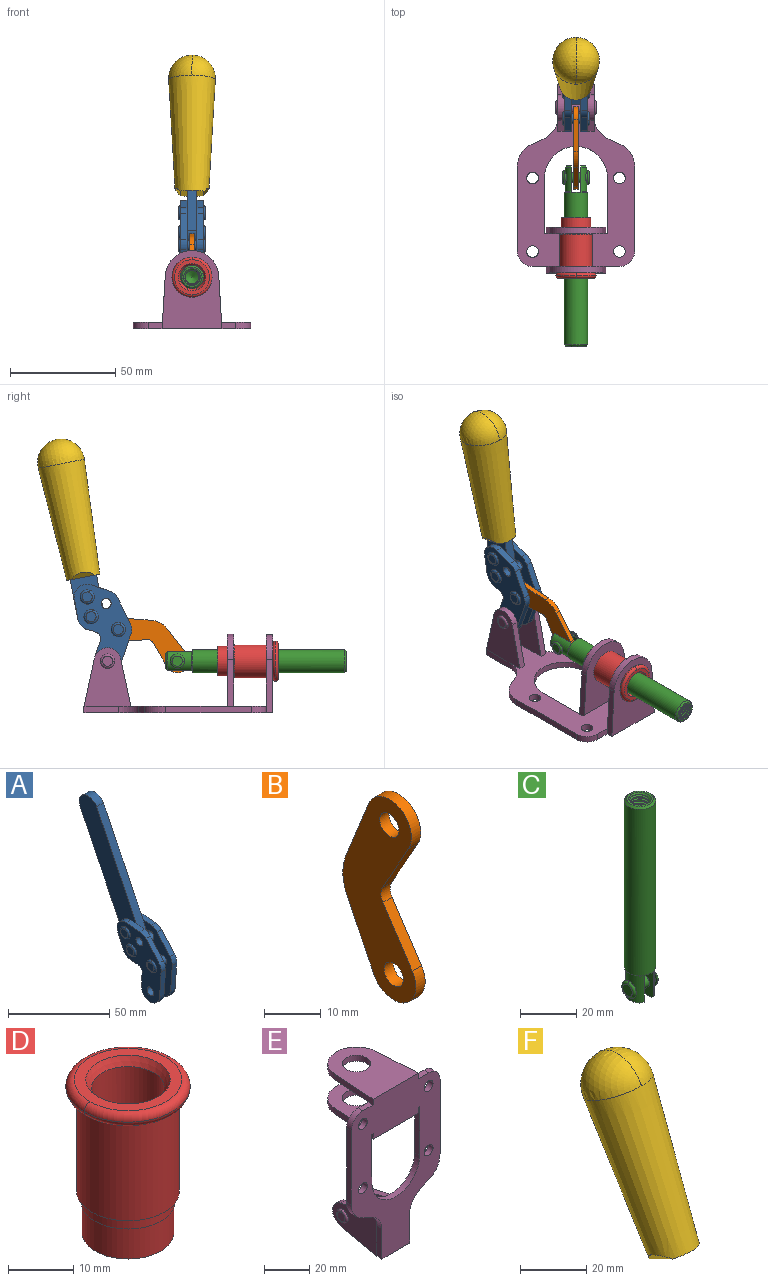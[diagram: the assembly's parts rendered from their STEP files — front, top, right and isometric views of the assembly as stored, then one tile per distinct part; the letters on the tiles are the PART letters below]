
ASSEMBLY  parts=6 mates=6
PART A: 59 faces, bbox 12.9x60.2x99.6 mm
  f0: torus R=2.39mm, axis (-1,0,0), area 14.9mm2, adj f20,f43,f51
  f1: torus R=2.39mm, axis (-1,0,0), area 14.9mm2, adj f19,f42,f51
  f2: torus R=2.39mm, axis (-1,0,0), area 14.9mm2, adj f18,f35,f51
  f3: torus R=2.39mm, axis (-1,0,0), area 14.9mm2, adj f14,f17,f23
  f4: torus R=2.39mm, axis (-1,0,0), area 14.9mm2, adj f13,f16,f23
  f5: torus R=2.39mm, axis (-1,0,0), area 14.9mm2, adj f12,f15,f23
  f6: cylinder r=2.39mm len=4.78mm, axis (1,0,0), area 46.5mm2, adj f48,f50,f51
  f7: cylinder r=2.39mm len=4.78mm, axis (1,0,0), area 46.5mm2, adj f50,f51
  f8: cylinder r=6.35mm len=12.68mm, axis (1,0,0), area 61.8mm2, adj f38,f39,f50,f51
  f9: cylinder r=2.39mm len=4.78mm, axis (-1,0,0), area 70.5mm2, adj f46,f50
  f10: cylinder r=2.39mm len=4.78mm, axis (-1,0,0), area 46.5mm2, adj f23,f45,f46
  f11: cylinder r=2.39mm len=4.78mm, axis (-1,0,0), area 46.5mm2, adj f23,f46
  f12: plane 4.78x4.78mm, normal (1,0,0), area 17.9mm2, adj f5,f15
  f13: plane 4.78x4.78mm, normal (1,0,0), area 17.9mm2, adj f4,f16
  f14: plane 4.78x4.78mm, normal (1,0,0), area 17.9mm2, adj f3,f17
  f15: torus R=2.39mm, axis (-1,0,0), area 14.9mm2, adj f5,f12,f23
  f16: torus R=2.39mm, axis (-1,0,0), area 14.9mm2, adj f4,f13,f23
  f17: torus R=2.39mm, axis (-1,0,0), area 14.9mm2, adj f3,f14,f23
  f18: plane 4.78x4.78mm, normal (-1,0,0), area 17.9mm2, adj f2,f35
  f19: plane 4.78x4.78mm, normal (-1,0,0), area 17.9mm2, adj f1,f42
  f20: plane 4.78x4.78mm, normal (-1,0,0), area 17.9mm2, adj f0,f43
  f21: plane 2.26x0.2mm, normal (1,0,0), area 0.2mm2, adj f31,f44
  f22: plane 2.26x0.2mm, normal (-1,0,0), area 0.2mm2, adj f41,f44
  f23: plane 39.37x30.77mm, normal (1,0,0), area 565.5mm2, adj f3,f4,f5,f10,f11,f15,f16,f17
  f24: cylinder r=6.1mm len=4.15mm, axis (-1,0,0), area 14.7mm2, adj f23,f25,f32,f46
  f25: plane 10.25x9.01mm, normal (0,-0.75,0.66), area 42.3mm2, adj f23,f24,f26,f46
  f26: cylinder r=6.35mm len=4.64mm, axis (-1,0,0), area 15.6mm2, adj f23,f25,f27,f46
  f27: plane 15.84x3.1mm, normal (0,-1,-0.07), area 49.2mm2, adj f23,f26,f28,f46
  f28: cylinder r=6.35mm len=12.68mm, axis (-1,0,0), area 61.8mm2, adj f23,f27,f29,f46
  f29: plane 8.11x3.1mm, normal (0,1,0.07), area 25.2mm2, adj f23,f28,f30,f46
  f30: cylinder r=3.05mm len=3.25mm, axis (-1,0,0), area 14.8mm2, adj f23,f29,f31,f46
  f31: plane 5.99x3.1mm, normal (0,0.07,-1), area 18.6mm2, adj f21,f23,f30,f44,f46
  f32: plane 9.5x3.1mm, normal (0,-0.07,1), area 29.5mm2, adj f23,f24,f33,f46,f47
  f33: cylinder r=6.1mm len=8.63mm, axis (-1,0,0), area 39.1mm2, adj f23,f32,f34,f47
  f34: plane 8.65x3.96mm, normal (0,0.91,-0.42), area 29.5mm2, adj f23,f33,f44,f47
  f35: torus R=2.39mm, axis (-1,0,0), area 14.9mm2, adj f2,f18,f51
  f36: plane 10.25x9.01mm, normal (0,-0.75,0.66), area 42.3mm2, adj f37,f49,f50,f51
  f37: cylinder r=6.35mm len=4.64mm, axis (1,0,0), area 15.6mm2, adj f36,f38,f50,f51
  f38: plane 15.84x3.1mm, normal (0,-1,-0.07), area 49.2mm2, adj f8,f37,f50,f51
  f39: plane 8.11x3.1mm, normal (0,1,0.07), area 25.2mm2, adj f8,f40,f50,f51
  f40: cylinder r=3.05mm len=3.25mm, axis (1,0,0), area 14.8mm2, adj f39,f41,f50,f51
  f41: plane 5.99x3.1mm, normal (0,0.07,-1), area 18.6mm2, adj f22,f40,f44,f50,f51
  f42: torus R=2.39mm, axis (-1,0,0), area 14.9mm2, adj f1,f19,f51
  f43: torus R=2.39mm, axis (-1,0,0), area 14.9mm2, adj f0,f20,f51
  f44: cylinder r=6.35mm len=12.12mm, axis (-1,0,0), area 128.9mm2, adj f21,f22,f23,f31,f34,f41,f46,f47
  f45: plane 2.65x1.35mm, normal (1,0,0), area 1mm2, adj f10,f55
  f46: plane 39.08x20.42mm, normal (-1,0,0), area 412.5mm2, adj f9,f10,f11,f24,f25,f26,f27,f28
  f47: plane 77.62x39.82mm, normal (1,0,0), area 850mm2, adj f32,f33,f34,f44,f53,f54,f55
  f48: plane 2.65x1.35mm, normal (-1,0,0), area 1mm2, adj f6,f55
  f49: cylinder r=6.1mm len=4.15mm, axis (1,0,0), area 14.7mm2, adj f36,f50,f51,f56
  f50: plane 39.08x20.42mm, normal (1,0,0), area 412.5mm2, adj f6,f7,f8,f9,f36,f37,f38,f39
  f51: plane 39.37x30.77mm, normal (-1,0,0), area 565.5mm2, adj f0,f1,f2,f6,f7,f8,f35,f36
  f52: plane 8.65x3.96mm, normal (0,0.91,-0.42), area 29.5mm2, adj f44,f51,f57,f58
  f53: plane 68.49x33.4mm, normal (0,0.9,-0.44), area 358.1mm2, adj f44,f47,f54,f58
  f54: cylinder r=6.35mm len=12.06mm, axis (1,0,0), area 93.7mm2, adj f47,f53,f55,f58
  f55: plane 68.49x33.4mm, normal (0,-0.9,0.44), area 358.1mm2, adj f44,f45,f46,f47,f48,f50,f54,f58
  f56: plane 9.5x3.1mm, normal (0,-0.07,1), area 29.5mm2, adj f49,f50,f51,f57,f58
  f57: cylinder r=6.1mm len=8.63mm, axis (1,0,0), area 39.1mm2, adj f51,f52,f56,f58
  f58: plane 77.62x39.82mm, normal (-1,0,0), area 850mm2, adj f44,f52,f53,f54,f55,f56,f57
PART B: 12 faces, bbox 2.3x18.2x42.8 mm
  f0: cylinder r=2.4mm len=4.8mm, axis (1,0,0), area 34.9mm2, adj f4,f11
  f1: cylinder r=10.41mm len=8.47mm, axis (1,0,0), area 20.2mm2, adj f4,f9,f10,f11
  f2: cylinder r=3.05mm len=3.16mm, axis (1,0,0), area 7.7mm2, adj f4,f6,f7,f11
  f3: cylinder r=2.4mm len=4.8mm, axis (1,0,0), area 34.9mm2, adj f4,f11
  f4: plane 42.81x18.23mm, normal (-1,0,0), area 414.1mm2, adj f0,f1,f2,f3,f5,f6,f7,f8
  f5: cylinder r=5.54mm len=10.67mm, axis (1,0,0), area 41.8mm2, adj f4,f6,f10,f11
  f6: plane 11.66x6.53mm, normal (0,-0.87,-0.49), area 30.9mm2, adj f2,f4,f5,f11
  f7: plane 11.17x7.33mm, normal (0,-0.84,0.55), area 30.9mm2, adj f2,f4,f8,f11
  f8: cylinder r=5.54mm len=10.51mm, axis (1,0,0), area 41.8mm2, adj f4,f7,f9,f11
  f9: plane 13.67x6.67mm, normal (0,0.9,-0.44), area 35.1mm2, adj f1,f4,f8,f11
  f10: plane 14.1x5.7mm, normal (0,0.93,0.37), area 35.1mm2, adj f1,f4,f5,f11
  f11: plane 42.81x18.23mm, normal (1,0,0), area 414.1mm2, adj f0,f1,f2,f3,f5,f6,f7,f8
PART C: 48 faces, bbox 12.6x11.1x86.1 mm
  f0: torus R=2.41mm, axis (-1,0,0), area 15mm2, adj f30,f32,f34
  f1: torus R=2.41mm, axis (-1,0,0), area 15mm2, adj f29,f31,f33
  f2: cylinder r=5.54mm len=72.39mm, axis (0,0,1), area 2518.5mm2, adj f3,f4,f42,f43
  f3: cone r=5.54mm half-angle=45deg, axis (0,0,1), area 7.6mm2, adj f2,f5,f41
  f4: cone r=5.54mm half-angle=45deg, axis (0,0,-1), area 34.9mm2, adj f2,f39
  f5: cylinder r=5.08mm len=11.48mm, axis (0,0,1), area 108.3mm2, adj f3,f7,f8,f41
  f6: cylinder r=2.41mm len=4.83mm, axis (-1,0,0), area 71.2mm2, adj f40,f41
  f7: cylinder r=2.41mm len=4.83mm, axis (-1,0,0), area 7.6mm2, adj f5,f34
  f8: cone r=5.08mm half-angle=45deg, axis (0,0,1), area 10.6mm2, adj f5,f37,f41
  f9: cone r=3.98mm half-angle=45deg, axis (0,0,1), area 17.6mm2, adj f27,f39,f45,f46,f47
  f10: cylinder r=2.41mm len=4.83mm, axis (-1,0,0), area 7.6mm2, adj f33,f38
  f11: cylinder r=3.2mm len=6.4mm, axis (0,0,1), area 78.4mm2, adj f12,f28,f44,f45,f47
  f12: cylinder r=3.2mm len=6.4mm, axis (0,0,1), area 10.5mm2, adj f11,f13,f45,f47
  f13: cylinder r=3.2mm len=6.4mm, axis (0,0,1), area 10.5mm2, adj f12,f14,f45,f47
  f14: cylinder r=3.2mm len=6.4mm, axis (0,0,1), area 10.5mm2, adj f13,f15,f45,f47
  f15: cylinder r=3.2mm len=6.4mm, axis (0,0,1), area 10.5mm2, adj f14,f16,f45,f47
  f16: cylinder r=3.2mm len=6.4mm, axis (0,0,1), area 10.5mm2, adj f15,f17,f45,f47
  f17: cylinder r=3.2mm len=6.4mm, axis (0,0,1), area 10.5mm2, adj f16,f18,f45,f47
  f18: cylinder r=3.2mm len=6.4mm, axis (0,0,1), area 10.5mm2, adj f17,f19,f45,f47
  f19: cylinder r=3.2mm len=6.4mm, axis (0,0,1), area 10.5mm2, adj f18,f20,f45,f47
  f20: cylinder r=3.2mm len=6.4mm, axis (0,0,1), area 10.5mm2, adj f19,f21,f45,f47
  f21: cylinder r=3.2mm len=6.4mm, axis (0,0,1), area 10.5mm2, adj f20,f22,f45,f47
  f22: cylinder r=3.2mm len=6.4mm, axis (0,0,1), area 10.5mm2, adj f21,f23,f45,f47
  f23: cylinder r=3.2mm len=6.4mm, axis (0,0,1), area 10.5mm2, adj f22,f24,f45,f47
  f24: cylinder r=3.2mm len=6.4mm, axis (0,0,1), area 10.5mm2, adj f23,f25,f45,f47
  f25: cylinder r=3.2mm len=6.4mm, axis (0,0,1), area 10.5mm2, adj f24,f26,f45,f47
  f26: cylinder r=3.2mm len=6.4mm, axis (0,0,1), area 10.5mm2, adj f25,f27,f45,f47
  f27: cylinder r=3.2mm len=6.4mm, axis (0,0,1), area 7.4mm2, adj f9,f26,f45,f47
  f28: cone r=3.2mm half-angle=60deg, axis (0,0,1), area 37.2mm2, adj f11
  f29: plane 4.83x4.83mm, normal (-1,0,0), area 18.3mm2, adj f1,f31
  f30: plane 4.83x4.83mm, normal (1,0,0), area 18.3mm2, adj f0,f32
  f31: torus R=2.41mm, axis (-1,0,0), area 15mm2, adj f1,f29,f33
  f32: torus R=2.41mm, axis (-1,0,0), area 15mm2, adj f0,f30,f34
  f33: plane 6.83x6.83mm, normal (1,0,0), area 18.3mm2, adj f1,f10,f31
  f34: plane 6.83x6.83mm, normal (-1,0,0), area 18.3mm2, adj f0,f7,f32
  f35: cone r=5.08mm half-angle=45deg, axis (0,0,1), area 10.6mm2, adj f36,f38,f40
  f36: plane 7.25x1.97mm, normal (0,0,-1), area 10mm2, adj f35,f40
  f37: plane 7.25x1.97mm, normal (0,0,-1), area 10mm2, adj f8,f41
  f38: cylinder r=5.08mm len=11.48mm, axis (0,0,1), area 108.3mm2, adj f10,f35,f40,f42
  f39: plane 9.55x9.55mm, normal (0,0,1), area 22mm2, adj f4,f9
  f40: plane 12.76x10.09mm, normal (1,0,0), area 95.7mm2, adj f6,f35,f36,f38,f42,f43
  f41: plane 12.76x10.09mm, normal (-1,0,0), area 95.7mm2, adj f3,f5,f6,f8,f37,f43
  f42: cone r=5.54mm half-angle=45deg, axis (0,0,1), area 7.6mm2, adj f2,f38,f40
  f43: plane 11.07x4.7mm, normal (0,0,-1), area 50.4mm2, adj f2,f40,f41
  f44: plane 0.89x0.62mm, normal (-1,0,0), area 0.3mm2, adj f11,f45,f46,f47
  f45: bspline ~24.8x7.63mm, area 266.6mm2, adj f9,f11,f12,f13,f14,f15,f16,f17
  f46: bspline ~24.87x7.63mm, area 73.6mm2, adj f9,f44,f45,f47
  f47: bspline ~24.98x7.63mm, area 272.5mm2, adj f9,f11,f12,f13,f14,f15,f16,f17
PART D: 15 faces, bbox 20.6x20.6x28.7 mm
  f0: torus R=8.26mm, axis (0,0,1), area 56.8mm2, adj f1,f10,f12
  f1: torus R=8.26mm, axis (0,0,1), area 56.8mm2, adj f0,f6,f13
  f2: cylinder r=5.59mm len=25.91mm, axis (0,0,1), area 909.6mm2, adj f3,f4
  f3: cone r=6.86mm half-angle=45deg, axis (0,0,-1), area 70.2mm2, adj f2,f14
  f4: cone r=6.47mm half-angle=30deg, axis (0,0,1), area 66.7mm2, adj f2,f13
  f5: cylinder r=7.04mm len=14.07mm, axis (0,0,1), area 252.6mm2, adj f11,f14
  f6: torus R=8.26mm, axis (0,0,1), area 56.8mm2, adj f1,f12,f13
  f7: cylinder r=7.16mm len=14.33mm, axis (0,0,1), area 91.5mm2, adj f9,f11
  f8: cylinder r=7.86mm len=18.42mm, axis (0,0,1), area 909.6mm2, adj f9,f10
  f9: plane 15.72x15.72mm, normal (0,0,-1), area 33mm2, adj f7,f8
  f10: plane 16.51x16.51mm, normal (0,0,-1), area 19.9mm2, adj f0,f8,f12
  f11: plane 14.33x14.33mm, normal (0,0,-1), area 5.7mm2, adj f5,f7
  f12: torus R=8.26mm, axis (0,0,1), area 56.8mm2, adj f0,f6,f10
  f13: plane 16.51x16.51mm, normal (0,0,1), area 82.7mm2, adj f1,f4,f6
  f14: plane 14.07x14.07mm, normal (0,0,-1), area 7.8mm2, adj f3,f5
PART E: 55 faces, bbox 55.7x37.4x89.8 mm
  f0: torus R=2.41mm, axis (-1,0,0), area 15mm2, adj f11,f15,f25
  f1: torus R=2.41mm, axis (-1,0,0), area 15mm2, adj f10,f12,f22
  f2: cylinder r=2.78mm len=5.56mm, axis (0,-1,0), area 54.2mm2, adj f30,f54
  f3: cylinder r=14.99mm len=29.97mm, axis (0,-1,0), area 145.9mm2, adj f30,f49,f53,f54
  f4: cylinder r=2.78mm len=5.56mm, axis (0,-1,0), area 54.2mm2, adj f30,f54
  f5: cylinder r=2.78mm len=5.56mm, axis (0,-1,0), area 54.2mm2, adj f30,f54
  f6: cylinder r=2.78mm len=5.56mm, axis (0,-1,0), area 54.2mm2, adj f30,f54
  f7: cylinder r=6.35mm len=12.7mm, axis (0,0,1), area 123.6mm2, adj f27,f51
  f8: cylinder r=6.35mm len=12.7mm, axis (0,0,-1), area 124.7mm2, adj f21,f35
  f9: cylinder r=2.41mm len=11.18mm, axis (-1,0,0), area 169.4mm2, adj f16,f19
  f10: plane 4.83x4.83mm, normal (1,0,0), area 18.3mm2, adj f1,f12
  f11: plane 4.83x4.83mm, normal (-1,0,0), area 18.3mm2, adj f0,f15
  f12: torus R=2.41mm, axis (-1,0,0), area 15mm2, adj f1,f10,f22
  f13: cylinder r=6.35mm len=12.41mm, axis (1,0,0), area 53.4mm2, adj f18,f19,f22,f23
  f14: cylinder r=6.35mm len=12.41mm, axis (-1,0,0), area 53.4mm2, adj f16,f17,f24,f25
  f15: torus R=2.41mm, axis (-1,0,0), area 15mm2, adj f0,f11,f25
  f16: plane 27.86x22.35mm, normal (1,0,0), area 425.4mm2, adj f9,f14,f17,f24,f30
  f17: plane 22.86x4.97mm, normal (0,0.21,0.98), area 72.5mm2, adj f14,f16,f25,f30
  f18: plane 22.86x4.97mm, normal (0,0.21,0.98), area 72.5mm2, adj f13,f19,f22,f30
  f19: plane 27.86x22.35mm, normal (-1,0,0), area 425.4mm2, adj f9,f13,f18,f23,f30
  f20: cylinder r=12.7mm len=25.35mm, axis (0,0,-1), area 119.8mm2, adj f21,f34,f35,f36
  f21: plane 34.21x28.07mm, normal (0,0,-1), area 702.4mm2, adj f8,f20,f30,f34,f36
  f22: plane 27.96x22.45mm, normal (1,0,0), area 407.2mm2, adj f1,f12,f13,f18,f23,f30,f42,f43
  f23: plane 22.86x4.97mm, normal (0,0.21,-0.98), area 72.5mm2, adj f13,f19,f22,f44
  f24: plane 22.86x4.97mm, normal (0,0.21,-0.98), area 72.5mm2, adj f14,f16,f25,f44
  f25: plane 27.86x22.35mm, normal (-1,0,0), area 407.1mm2, adj f0,f14,f15,f17,f24,f30,f45,f46
  f26: plane 3.1x0.95mm, normal (0,0,-1), area 2.7mm2, adj f30,f49,f50,f54
  f27: plane 34.21x28.07mm, normal (0,0,1), area 702.4mm2, adj f7,f28,f30,f50,f52
  f28: cylinder r=12.7mm len=25.35mm, axis (0,0,1), area 118.8mm2, adj f27,f50,f51,f52
  f29: plane 3.1x0.95mm, normal (0,0,-1), area 2.7mm2, adj f30,f52,f53,f54
  f30: plane 86.54x55.63mm, normal (0,1,0), area 2362.9mm2, adj f2,f3,f4,f5,f6,f16,f17,f18
  f31: plane 40.56x3.1mm, normal (-1,0,0), area 125.7mm2, adj f30,f32,f48,f54
  f32: cylinder r=7.11mm len=7.11mm, axis (0,-1,0), area 34.6mm2, adj f30,f31,f33,f54
  f33: plane 6.67x3.1mm, normal (0,0,1), area 20.4mm2, adj f30,f32,f34,f54
  f34: plane 25.39x3.13mm, normal (-1,0.06,0), area 79.5mm2, adj f20,f21,f33,f35,f54
  f35: plane 37.31x28.45mm, normal (0,0,1), area 789.9mm2, adj f8,f20,f34,f36,f54
  f36: plane 25.39x3.13mm, normal (1,0.06,0), area 79.5mm2, adj f20,f21,f35,f37,f54
  f37: plane 6.67x3.1mm, normal (0,0,1), area 20.4mm2, adj f30,f36,f38,f54
  f38: cylinder r=7.11mm len=7.11mm, axis (0,-1,0), area 34.6mm2, adj f30,f37,f39,f54
  f39: plane 40.56x3.1mm, normal (1,0,0), area 125.7mm2, adj f30,f38,f40,f54
  f40: cylinder r=11.18mm len=10.16mm, axis (0,-1,0), area 39.5mm2, adj f30,f39,f41,f54
  f41: plane 6.09x3.1mm, normal (0.42,0,-0.91), area 20.8mm2, adj f30,f40,f42,f54
  f42: cylinder r=11.18mm len=9.41mm, axis (0,-1,0), area 37.2mm2, adj f22,f30,f41,f43,f54
  f43: plane 16.5x3.1mm, normal (1,0,0), area 51.1mm2, adj f22,f42,f44,f54
  f44: plane 17.37x3.1mm, normal (0,0,-1), area 53.8mm2, adj f23,f24,f30,f43,f45,f54
  f45: plane 16.5x3.1mm, normal (-1,0,0), area 51.1mm2, adj f25,f44,f46,f54
  f46: cylinder r=11.18mm len=9.41mm, axis (0,-1,0), area 37.2mm2, adj f25,f30,f45,f47,f54
  f47: plane 6.09x3.1mm, normal (-0.42,0,-0.91), area 20.8mm2, adj f30,f46,f48,f54
  f48: cylinder r=11.18mm len=10.16mm, axis (0,-1,0), area 39.5mm2, adj f30,f31,f47,f54
  f49: plane 26.54x3.1mm, normal (-1,0,0), area 82.3mm2, adj f3,f26,f30,f54
  f50: plane 25.39x3.1mm, normal (1,0.06,0), area 78.8mm2, adj f26,f27,f28,f51,f54
  f51: plane 37.31x28.45mm, normal (0,0,-1), area 789.9mm2, adj f7,f28,f50,f52,f54
  f52: plane 25.39x3.1mm, normal (-1,0.06,0), area 78.8mm2, adj f27,f28,f29,f51,f54
  f53: plane 26.54x3.1mm, normal (1,0,0), area 82.3mm2, adj f3,f29,f30,f54
  f54: plane 89.66x55.63mm, normal (0,-1,0), area 2678.5mm2, adj f2,f3,f4,f5,f6,f26,f29,f31
PART F: 11 faces, bbox 22.3x42.6x64.5 mm
  f0: sphere r=11.13mm, area 411.4mm2, adj f1,f8
  f1: cone r=11.11mm half-angle=3.3deg, axis (0,0.44,0.9), area 3251.8mm2, adj f0,f7,f8,f9,f10
  f2: cylinder r=6.16mm len=11.7mm, axis (1,0,0), area 89.5mm2, adj f3,f4,f5,f6
  f3: plane 60.23x36.75mm, normal (-1,0,0), area 763.6mm2, adj f2,f4,f6,f10
  f4: plane 51.37x25.05mm, normal (0,0.9,-0.44), area 264.2mm2, adj f2,f3,f5,f10
  f5: plane 60.23x36.75mm, normal (1,0,0), area 763.6mm2, adj f2,f4,f6,f10
  f6: plane 51.37x25.05mm, normal (0,-0.9,0.44), area 264.2mm2, adj f2,f3,f5,f10
  f7: plane 9.95x5.95mm, normal (0.71,-0.31,-0.64), area 25.8mm2, adj f1,f10
  f8: sphere r=11.13mm, area 411.4mm2, adj f0,f1
  f9: plane 9.95x5.95mm, normal (-0.71,-0.31,-0.64), area 25.8mm2, adj f1,f10
  f10: plane 14.27x11.38mm, normal (0,-0.44,-0.9), area 106.7mm2, adj f1,f3,f4,f5,f6,f7,f9
PLACE A rot(axis=(1,0,0),15deg) t=(0,9.44,49.24)mm
PLACE B rot(axis=(1,0,0),120.2deg) t=(0,34.13,11.13)mm
PLACE C rot(axis=(0,-0.71,0.71),180deg) t=(0,23.85,49.23)mm
PLACE D rot(axis=(0.58,0.58,-0.58),120deg) t=(-24.61,9.43,24.61)mm
PLACE E rot(axis=(1,0,0),90deg) t=(0,9.43,0)mm fixed
PLACE F rot(axis=(1,0,0),15deg) t=(0,9.44,49.24)mm
MATE revolute B.f3 <-> A.f4  axis (1,0,0) through (0,36.35,39.62)mm
MATE fastened D.f2 <-> E.f7  axis (0,-1,0) through (0,-36.96,24.61)mm
MATE revolute C.f6 <-> B.f5  axis (1,0,0) through (0,8.38,24.61)mm
MATE slider C.f2 <-> D.f2  axis (0,-1,0) through (0,-34.93,24.61)mm
MATE fastened F.f2 <-> A.f54  axis (1,0,0) through (0,63.89,120.54)mm
MATE revolute A.f7 <-> E.f0  axis (-1,0,0) through (0,41.52,24.61)mm
